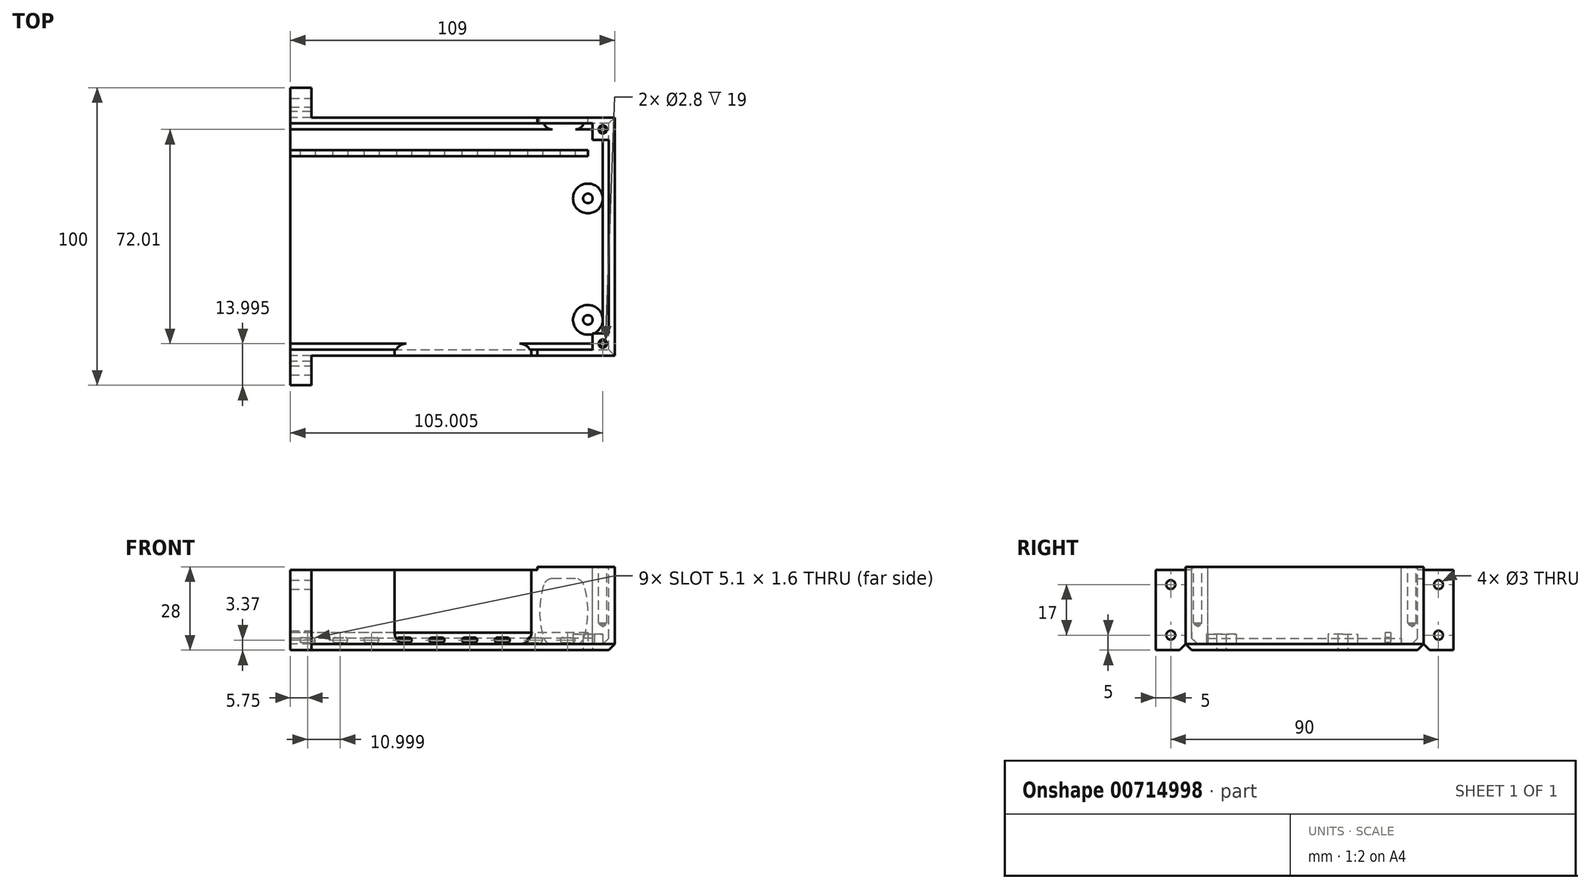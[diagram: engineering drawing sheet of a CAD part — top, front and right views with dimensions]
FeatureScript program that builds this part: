
annotation { "Feature Type Name" : "Feature", "Feature Type Description" : "" }
export const myFeature = defineFeature(function(context is Context, id is Id, definition is map)
    precondition{}
    {
        {
            var Q0;
            Q0=qCreatedBy(makeId("Top.planeOp"),FACE);
            var sketch = newSketch(context, id + "F0", { "sketchPlane" : qUnion([Q0])});
            skLineSegment(sketch, "E0.bottom", {"start": v(54.5, 40) * mm, "end": v(-54.5, 40) * mm});
            skLineSegment(sketch, "E0.top", {"start": v(54.5, -40) * mm, "end": v(-54.5, -40) * mm});
            skLineSegment(sketch, "E0.left", {"start": v(54.5, 40) * mm, "end": v(54.5, -40) * mm});
            skLineSegment(sketch, "E0.right", {"start": v(-54.5, 40) * mm, "end": v(-54.5, -40) * mm});
            skPoint(sketch, "E0.middle", {"position": v(0, 0) * mm});
            skSolve(sketch);
        }
        {
            var Q0;
            Q0=makeQuery(id+"F0.imprint","IMPRINT",FACE,{"disambiguationData":[TD([[makeQuery(id+"F0.imprint","IMPRINT",EDGE,{"derivedFrom":sQuery(id+"F0.wireOp",EDGE,"E0.bottom")}),1.0]])]});
            extrude(context, id + "F1", {"entities" : qUnion([Q0]), "depth" : 27 * mm, "offsetDistance" : 25 * mm});
        }
        {
            var Q0;
            Q0=makeQuery(id+"F1.opExtrude","SWEPT_FACE",FACE,{"disambiguationData":[OSD([sQuery(id+"F0.wireOp",EDGE,"E0.bottom")])]});
            var sketch = newSketch(context, id + "F2", { "sketchPlane" : qUnion([Q0])});
            skLineSegment(sketch, "E1.bottom", {"start": v(-54.5, 27) * mm, "end": v(-47.5, 27) * mm});
            skLineSegment(sketch, "E1.top", {"start": v(-54.5, 0) * mm, "end": v(-47.5, 0) * mm});
            skLineSegment(sketch, "E1.left", {"start": v(-54.5, 27) * mm, "end": v(-54.5, 0) * mm});
            skLineSegment(sketch, "E1.right", {"start": v(-47.5, 27) * mm, "end": v(-47.5, 0) * mm});
            skSolve(sketch);
        }
        {
            var Q0;
            Q0=makeQuery(id+"F2.imprint","IMPRINT",FACE,{"disambiguationData":[TD([[makeQuery(id+"F2.imprint","IMPRINT",EDGE,{"derivedFrom":sQuery(id+"F2.wireOp",EDGE,"E1.bottom")}),-1.0]])]});
            extrude(context, id + "F3", {"entities" : qUnion([Q0]), "operationType" : NewBodyOperationType.ADD, "depth" : 10 * mm, "offsetDistance" : 25 * mm});
        }
        {
            var Q0;
            Q0=makeQuery(id+"F1.opExtrude","SWEPT_FACE",FACE,{"disambiguationData":[OSD([sQuery(id+"F0.wireOp",EDGE,"E0.top")])]});
            var sketch = newSketch(context, id + "F4", { "sketchPlane" : qUnion([Q0])});
            skLineSegment(sketch, "E2.bottom", {"start": v(54.5, 27) * mm, "end": v(47.5, 27) * mm});
            skLineSegment(sketch, "E2.top", {"start": v(54.5, 0) * mm, "end": v(47.5, 0) * mm});
            skLineSegment(sketch, "E2.left", {"start": v(54.5, 27) * mm, "end": v(54.5, 0) * mm});
            skLineSegment(sketch, "E2.right", {"start": v(47.5, 27) * mm, "end": v(47.5, 0) * mm});
            skSolve(sketch);
        }
        {
            var Q0;
            Q0=qSketchRegion(id+"F4",true);
            extrude(context, id + "F5", {"entities" : qUnion([Q0]), "operationType" : NewBodyOperationType.ADD, "depth" : 10 * mm, "offsetDistance" : 25 * mm});
        }
        {
            var Q0;
            Q0=makeQuery(id+"F5.boolean.opBoolean","MERGE",FACE,{"derivedFrom":[makeQuery(id+"F3.boolean.opBoolean","MERGE",FACE,{"derivedFrom":[makeQuery(id+"F1.opExtrude","CAP_FACE",FACE,{"disambiguationData":[OSD([sQuery(id+"F0.wireOp",EDGE,"E0.bottom"),sQuery(id+"F0.wireOp",EDGE,"E0.top"),sQuery(id+"F0.wireOp",EDGE,"E0.left"),sQuery(id+"F0.wireOp",EDGE,"E0.right")])],"isStart":false}),makeQuery(id+"F3.opExtrude","SWEPT_FACE",FACE,{"disambiguationData":[OSD([sQuery(id+"F2.wireOp",EDGE,"E1.bottom")])]})]}),makeQuery(id+"F5.opExtrude","SWEPT_FACE",FACE,{"disambiguationData":[OSD([sQuery(id+"F4.wireOp",EDGE,"E2.bottom")])]})]});
            var sketch = newSketch(context, id + "F6", { "sketchPlane" : qUnion([Q0])});
            skLineSegment(sketch, "E3.0", {"start": v(-52.5, 32.5) * mm, "end": v(-52.5, -32.5) * mm});
            skLineSegment(sketch, "E3.1", {"start": v(52.5, 38) * mm, "end": v(-47, 38) * mm});
            skLineSegment(sketch, "E3.2", {"start": v(-47, -38) * mm, "end": v(54.24, -38) * mm});
            skPoint(sketch, "E4.orphan", {"position": v(49.5, 38) * mm});
            skLineSegment(sketch, "E5.top", {"start": v(-52.5, 32.5) * mm, "end": v(-47, 32.5) * mm});
            skLineSegment(sketch, "E5.right", {"start": v(-47, 38) * mm, "end": v(-47, 32.5) * mm});
            skLineSegment(sketch, "E6.top", {"start": v(-52.5, -32.5) * mm, "end": v(-47, -32.5) * mm});
            skLineSegment(sketch, "E6.right", {"start": v(-47, -38) * mm, "end": v(-47, -32.5) * mm});
            skLineSegment(sketch, "E7", {"start": v(54.24, -38) * mm, "end": v(54.5, -38) * mm});
            skLineSegment(sketch, "E8", {"start": v(52.5, 38) * mm, "end": v(54.5, 38) * mm});
            skSolve(sketch);
        }
        {
            var Q0;
            Q0=makeQuery(id+"F6.imprint","IMPRINT",FACE,{"disambiguationData":[TD([[makeQuery(id+"F6.imprint","IMPRINT",EDGE,{"derivedFrom":sQuery(id+"F6.wireOp",EDGE,"E3.0")}),1.0]])]});
            extrude(context, id + "F7", {"entities" : qUnion([Q0]), "operationType" : NewBodyOperationType.REMOVE, "oppositeDirection" : true, "depth" : 25 * mm, "offsetDistance" : 25 * mm});
        }
        {
            var Q0;
            Q0=makeQuery(id+"F5.boolean.opBoolean","MERGE",FACE,{"derivedFrom":[makeQuery(id+"F3.boolean.opBoolean","MERGE",FACE,{"derivedFrom":[makeQuery(id+"F1.opExtrude","CAP_FACE",FACE,{"disambiguationData":[OSD([sQuery(id+"F0.wireOp",EDGE,"E0.bottom"),sQuery(id+"F0.wireOp",EDGE,"E0.top"),sQuery(id+"F0.wireOp",EDGE,"E0.left"),sQuery(id+"F0.wireOp",EDGE,"E0.right")])],"isStart":true}),makeQuery(id+"F3.opExtrude","SWEPT_FACE",FACE,{"disambiguationData":[OSD([sQuery(id+"F2.wireOp",EDGE,"E1.top")])]})]}),makeQuery(id+"F5.opExtrude","SWEPT_FACE",FACE,{"disambiguationData":[OSD([sQuery(id+"F4.wireOp",EDGE,"E2.top")])]})]});
            var sketch = newSketch(context, id + "F8", { "sketchPlane" : qUnion([Q0])});
            skLineSegment(sketch, "E9.bottom", {"start": v(54.5, 40) * mm, "end": v(-45.5, 40) * mm, "construction": true});
            skLineSegment(sketch, "E9.top", {"start": v(54.5, -40) * mm, "end": v(-45.5, -40) * mm, "construction": true});
            skLineSegment(sketch, "E9.left", {"start": v(54.5, 40) * mm, "end": v(54.5, -40) * mm, "construction": true});
            skLineSegment(sketch, "E9.right", {"start": v(-45.5, 40) * mm, "end": v(-45.5, -40) * mm, "construction": true});
            skLineSegment(sketch, "E10", {"start": v(-45.5, 40) * mm, "end": v(-45.5, 28) * mm, "construction": true});
            skLineSegment(sketch, "E11", {"start": v(-45.5, 40) * mm, "end": v(-45.5, -12.8) * mm, "construction": true});
            skCircle(sketch, "E12", {"center": v(-45.5, 28) * mm, "radius": 1.6 * mm});
            skCircle(sketch, "E13", {"center": v(-45.5, -12.8) * mm, "radius": 1.6 * mm});
            skCircle(sketch, "E14", {"center": v(-45.5, 28) * mm, "radius": 5 * mm});
            skCircle(sketch, "E15", {"center": v(-45.5, -12.8) * mm, "radius": 5 * mm});
            skSolve(sketch);
        }
        {
            var Q0;
            Q0=sQuery(id+"F8.wireOp",VERTEX,"E10.end");
            var Q1;
            Q1=sQuery(id+"F8.wireOp",VERTEX,"E11.end");
            var Q2;
            Q2=makeQuery(id+"F1.opExtrude","SWEPT_BODY",BODY,{"disambiguationData":[OSD([sQuery(id+"F0.wireOp",EDGE,"E0.bottom"),sQuery(id+"F0.wireOp",EDGE,"E0.top"),sQuery(id+"F0.wireOp",EDGE,"E0.left"),sQuery(id+"F0.wireOp",EDGE,"E0.right")])]});
            hole(context, id + "F9", {"style" : HoleStyle.SIMPLE, "endStyle" : HoleEndStyle.THROUGH, "holeDiameter" : 3.2 * mm, "majorDiameter" : 5 * mm, "isTappedThrough" : true, "tappedDepth" : 12 * mm, "tapClearance" : 3, "startFromSketch" : true, "locations" : qUnion([Q0, Q1]), "scope" : qUnion([Q2])});
        }
        {
            var Q0;
            Q0=makeQuery(id+"F7.boolean.opBoolean","COPY",FACE,{"derivedFrom":makeQuery(id+"F7.opExtrude","CAP_FACE",FACE,{"disambiguationData":[OSD([sQuery(id+"F0.wireOp",EDGE,"E0.left"),sQuery(id+"F2.wireOp",EDGE,"E1.bottom"),sQuery(id+"F2.wireOp",EDGE,"E1.left"),sQuery(id+"F4.wireOp",EDGE,"E2.bottom"),sQuery(id+"F4.wireOp",EDGE,"E2.left"),sQuery(id+"F6.wireOp",EDGE,"E3.0"),sQuery(id+"F6.wireOp",EDGE,"E3.1"),sQuery(id+"F6.wireOp",EDGE,"E3.2"),sQuery(id+"F6.wireOp",EDGE,"E5.top"),sQuery(id+"F6.wireOp",EDGE,"E5.right"),sQuery(id+"F6.wireOp",EDGE,"E6.top"),sQuery(id+"F6.wireOp",EDGE,"E6.right"),sQuery(id+"F6.wireOp",EDGE,"E7"),sQuery(id+"F6.wireOp",EDGE,"E8")])],"isStart":false})});
            var sketch = newSketch(context, id + "F10", { "sketchPlane" : qUnion([Q0])});
            skLineSegment(sketch, "E16.bottom", {"start": v(54.5, 38) * mm, "end": v(-47, 38) * mm, "construction": true});
            skLineSegment(sketch, "E16.top", {"start": v(54.5, 29) * mm, "end": v(-47, 29) * mm, "construction": true});
            skLineSegment(sketch, "E16.left", {"start": v(54.5, 38) * mm, "end": v(54.5, 29) * mm, "construction": true});
            skLineSegment(sketch, "E16.right", {"start": v(-47, 38) * mm, "end": v(-47, 29) * mm, "construction": true});
            skLineSegment(sketch, "E17", {"start": v(-52.5, 29) * mm, "end": v(-45.5, 29) * mm, "construction": true});
            skLineSegment(sketch, "E18.bottom", {"start": v(-45.5, 29) * mm, "end": v(54.5, 29) * mm});
            skLineSegment(sketch, "E18.top", {"start": v(-45.5, 27) * mm, "end": v(54.5, 27) * mm});
            skLineSegment(sketch, "E18.left", {"start": v(-45.5, 29) * mm, "end": v(-45.5, 27) * mm});
            skLineSegment(sketch, "E18.right", {"start": v(54.5, 29) * mm, "end": v(54.5, 27) * mm});
            skSolve(sketch);
        }
        {
            var Q0;
            Q0=qSketchRegion(id+"F10",true);
            extrude(context, id + "F11", {"entities" : qUnion([Q0]), "operationType" : NewBodyOperationType.ADD, "depth" : 3.9 * mm, "offsetDistance" : 25 * mm});
        }
        {
            var Q0;
            Q0=makeQuery(id+"F11.opExtrude","SWEPT_FACE",FACE,{"disambiguationData":[OSD([sQuery(id+"F10.wireOp",EDGE,"E18.top")])]});
            var sketch = newSketch(context, id + "F12", { "sketchPlane" : qUnion([Q0])});
            skLineSegment(sketch, "E19.bottom", {"start": v(54.5, 5.9) * mm, "end": v(-45.5, 5.9) * mm, "construction": true});
            skLineSegment(sketch, "E19.top", {"start": v(54.5, 3.37) * mm, "end": v(-45.5, 3.37) * mm, "construction": true});
            skLineSegment(sketch, "E19.left", {"start": v(54.5, 5.9) * mm, "end": v(54.5, 3.37) * mm, "construction": true});
            skLineSegment(sketch, "E19.right", {"start": v(-45.5, 5.9) * mm, "end": v(-45.5, 3.37) * mm, "construction": true});
            skLineSegment(sketch, "E20", {"start": v(54.5, 3.37) * mm, "end": v(48.75, 3.37) * mm, "construction": true});
            skLineSegment(sketch, "E21.bottom", {"start": v(50.5, 4.17) * mm, "end": v(47, 4.17) * mm});
            skLineSegment(sketch, "E21.top", {"start": v(50.5, 2.57) * mm, "end": v(47, 2.57) * mm});
            skPoint(sketch, "E21.middle", {"position": v(48.75, 3.37) * mm});
            skArc(sketch, "E22", {"start": v(47, 4.17) * mm, "mid": v(46.2, 3.37) * mm, "end": v(47, 2.57) * mm});
            skArc(sketch, "E23", {"start": v(50.5, 2.57) * mm, "mid": v(51.3, 3.37) * mm, "end": v(50.5, 4.17) * mm});
            skLineSegment(sketch, "E24", {"start": v(48.75, 3.37) * mm, "end": v(37.75, 3.37) * mm, "construction": true});
            skLineSegment(sketch, "E25.bottom", {"start": v(39.5, 4.17) * mm, "end": v(36, 4.17) * mm});
            skLineSegment(sketch, "E25.top", {"start": v(39.5, 2.57) * mm, "end": v(36, 2.57) * mm});
            skPoint(sketch, "E25.middle", {"position": v(37.75, 3.37) * mm});
            skArc(sketch, "E26", {"start": v(36, 4.17) * mm, "mid": v(35.2, 3.37) * mm, "end": v(36, 2.57) * mm});
            skArc(sketch, "E27", {"start": v(39.5, 2.57) * mm, "mid": v(40.3, 3.37) * mm, "end": v(39.5, 4.17) * mm});
            skLineSegment(sketch, "E28", {"start": v(37.75, 3.37) * mm, "end": v(26.75, 3.37) * mm, "construction": true});
            skLineSegment(sketch, "E29", {"start": v(26.75, 3.37) * mm, "end": v(15.75, 3.37) * mm, "construction": true});
            skLineSegment(sketch, "E30", {"start": v(15.75, 3.37) * mm, "end": v(4.75, 3.37) * mm, "construction": true});
            skLineSegment(sketch, "E31", {"start": v(4.75, 3.37) * mm, "end": v(-6.25, 3.37) * mm, "construction": true});
            skLineSegment(sketch, "E32", {"start": v(-6.25, 3.37) * mm, "end": v(-17.25, 3.37) * mm, "construction": true});
            skLineSegment(sketch, "E33", {"start": v(-17.25, 3.37) * mm, "end": v(-28.25, 3.37) * mm, "construction": true});
            skLineSegment(sketch, "E34", {"start": v(-28.25, 3.37) * mm, "end": v(-39.25, 3.37) * mm, "construction": true});
            skLineSegment(sketch, "E35.bottom", {"start": v(29.03, 4.17) * mm, "end": v(25.53, 4.17) * mm});
            skLineSegment(sketch, "E35.top", {"start": v(29.03, 2.57) * mm, "end": v(25.53, 2.57) * mm});
            skPoint(sketch, "E35.middle", {"position": v(27.28, 3.37) * mm});
            skArc(sketch, "E36", {"start": v(25.53, 4.17) * mm, "mid": v(24.73, 3.37) * mm, "end": v(25.53, 2.57) * mm});
            skArc(sketch, "E37", {"start": v(29.03, 2.57) * mm, "mid": v(29.83, 3.37) * mm, "end": v(29.03, 4.17) * mm});
            skLineSegment(sketch, "E38.bottom", {"start": v(18.03, 4.17) * mm, "end": v(14.53, 4.17) * mm});
            skLineSegment(sketch, "E38.top", {"start": v(18.03, 2.57) * mm, "end": v(14.53, 2.57) * mm});
            skPoint(sketch, "E38.middle", {"position": v(16.28, 3.37) * mm});
            skArc(sketch, "E39", {"start": v(14.53, 4.17) * mm, "mid": v(13.73, 3.37) * mm, "end": v(14.53, 2.57) * mm});
            skArc(sketch, "E40", {"start": v(18.03, 2.57) * mm, "mid": v(18.83, 3.37) * mm, "end": v(18.03, 4.17) * mm});
            skLineSegment(sketch, "E41.bottom", {"start": v(7.03, 4.17) * mm, "end": v(3.53, 4.17) * mm});
            skLineSegment(sketch, "E41.top", {"start": v(7.03, 2.57) * mm, "end": v(3.53, 2.57) * mm});
            skPoint(sketch, "E41.middle", {"position": v(5.28, 3.37) * mm});
            skArc(sketch, "E42", {"start": v(3.53, 4.17) * mm, "mid": v(2.73, 3.37) * mm, "end": v(3.53, 2.57) * mm});
            skArc(sketch, "E43", {"start": v(7.03, 2.57) * mm, "mid": v(7.83, 3.37) * mm, "end": v(7.03, 4.17) * mm});
            skLineSegment(sketch, "E44.bottom", {"start": v(-3.97, 4.17) * mm, "end": v(-7.47, 4.17) * mm});
            skLineSegment(sketch, "E44.top", {"start": v(-3.97, 2.57) * mm, "end": v(-7.47, 2.57) * mm});
            skPoint(sketch, "E44.middle", {"position": v(-5.72, 3.37) * mm});
            skArc(sketch, "E45", {"start": v(-7.47, 4.17) * mm, "mid": v(-8.27, 3.37) * mm, "end": v(-7.47, 2.57) * mm});
            skArc(sketch, "E46", {"start": v(-3.97, 2.57) * mm, "mid": v(-3.17, 3.37) * mm, "end": v(-3.97, 4.17) * mm});
            skLineSegment(sketch, "E47.bottom", {"start": v(-14.97, 4.17) * mm, "end": v(-18.47, 4.17) * mm});
            skLineSegment(sketch, "E47.top", {"start": v(-14.97, 2.57) * mm, "end": v(-18.47, 2.57) * mm});
            skPoint(sketch, "E47.middle", {"position": v(-16.72, 3.37) * mm});
            skArc(sketch, "E48", {"start": v(-18.47, 4.17) * mm, "mid": v(-19.27, 3.37) * mm, "end": v(-18.47, 2.57) * mm});
            skArc(sketch, "E49", {"start": v(-14.97, 2.57) * mm, "mid": v(-14.17, 3.37) * mm, "end": v(-14.97, 4.17) * mm});
            skLineSegment(sketch, "E50.bottom", {"start": v(-25.97, 4.17) * mm, "end": v(-29.47, 4.17) * mm});
            skLineSegment(sketch, "E50.top", {"start": v(-25.97, 2.57) * mm, "end": v(-29.47, 2.57) * mm});
            skPoint(sketch, "E50.middle", {"position": v(-27.72, 3.37) * mm});
            skArc(sketch, "E51", {"start": v(-29.47, 4.17) * mm, "mid": v(-30.27, 3.37) * mm, "end": v(-29.47, 2.57) * mm});
            skArc(sketch, "E52", {"start": v(-25.97, 2.57) * mm, "mid": v(-25.17, 3.37) * mm, "end": v(-25.97, 4.17) * mm});
            skLineSegment(sketch, "E53.bottom", {"start": v(-36.97, 4.17) * mm, "end": v(-40.47, 4.17) * mm});
            skLineSegment(sketch, "E53.top", {"start": v(-36.97, 2.57) * mm, "end": v(-40.47, 2.57) * mm});
            skPoint(sketch, "E53.middle", {"position": v(-38.72, 3.37) * mm});
            skArc(sketch, "E54", {"start": v(-40.47, 4.17) * mm, "mid": v(-41.27, 3.37) * mm, "end": v(-40.47, 2.57) * mm});
            skArc(sketch, "E55", {"start": v(-36.97, 2.57) * mm, "mid": v(-36.17, 3.37) * mm, "end": v(-36.97, 4.17) * mm});
            skSolve(sketch);
        }
        {
            var Q0;
            Q0=makeQuery(id+"F12.imprint","IMPRINT",FACE,{"disambiguationData":[TD([[makeQuery(id+"F12.imprint","IMPRINT",EDGE,{"derivedFrom":sQuery(id+"F12.wireOp",EDGE,"E53.bottom")}),1.0]])]});
            var Q1;
            Q1=makeQuery(id+"F12.imprint","IMPRINT",FACE,{"disambiguationData":[TD([[makeQuery(id+"F12.imprint","IMPRINT",EDGE,{"derivedFrom":sQuery(id+"F12.wireOp",EDGE,"E50.bottom")}),1.0]])]});
            var Q2;
            Q2=makeQuery(id+"F12.imprint","IMPRINT",FACE,{"disambiguationData":[TD([[makeQuery(id+"F12.imprint","IMPRINT",EDGE,{"derivedFrom":sQuery(id+"F12.wireOp",EDGE,"E47.bottom")}),1.0]])]});
            var Q3;
            Q3=makeQuery(id+"F12.imprint","IMPRINT",FACE,{"disambiguationData":[TD([[makeQuery(id+"F12.imprint","IMPRINT",EDGE,{"derivedFrom":sQuery(id+"F12.wireOp",EDGE,"E44.bottom")}),1.0]])]});
            var Q4;
            Q4=makeQuery(id+"F12.imprint","IMPRINT",FACE,{"disambiguationData":[TD([[makeQuery(id+"F12.imprint","IMPRINT",EDGE,{"derivedFrom":sQuery(id+"F12.wireOp",EDGE,"E41.bottom")}),1.0]])]});
            var Q5;
            Q5=makeQuery(id+"F12.imprint","IMPRINT",FACE,{"disambiguationData":[TD([[makeQuery(id+"F12.imprint","IMPRINT",EDGE,{"derivedFrom":sQuery(id+"F12.wireOp",EDGE,"E38.bottom")}),1.0]])]});
            var Q6;
            Q6=makeQuery(id+"F12.imprint","IMPRINT",FACE,{"disambiguationData":[TD([[makeQuery(id+"F12.imprint","IMPRINT",EDGE,{"derivedFrom":sQuery(id+"F12.wireOp",EDGE,"E35.bottom")}),1.0]])]});
            var Q7;
            Q7=makeQuery(id+"F12.imprint","IMPRINT",FACE,{"disambiguationData":[TD([[makeQuery(id+"F12.imprint","IMPRINT",EDGE,{"derivedFrom":sQuery(id+"F12.wireOp",EDGE,"E25.bottom")}),1.0]])]});
            var Q8;
            Q8=makeQuery(id+"F12.imprint","IMPRINT",FACE,{"disambiguationData":[TD([[makeQuery(id+"F12.imprint","IMPRINT",EDGE,{"derivedFrom":sQuery(id+"F12.wireOp",EDGE,"E21.bottom")}),1.0]])]});
            extrude(context, id + "F13", {"entities" : qUnion([Q0, Q1, Q2, Q3, Q4, Q5, Q6, Q7, Q8]), "operationType" : NewBodyOperationType.REMOVE, "endBound" : BoundingType.UP_TO_NEXT, "oppositeDirection" : true, "depth" : 25 * mm, "offsetDistance" : 25 * mm});
        }
        {
            var Q0;
            Q0=makeQuery(id+"F7.boolean.opBoolean","COPY",FACE,{"derivedFrom":makeQuery(id+"F7.opExtrude","CAP_FACE",FACE,{"disambiguationData":[OSD([sQuery(id+"F0.wireOp",EDGE,"E0.left"),sQuery(id+"F2.wireOp",EDGE,"E1.bottom"),sQuery(id+"F2.wireOp",EDGE,"E1.left"),sQuery(id+"F4.wireOp",EDGE,"E2.bottom"),sQuery(id+"F4.wireOp",EDGE,"E2.left"),sQuery(id+"F6.wireOp",EDGE,"E3.0"),sQuery(id+"F6.wireOp",EDGE,"E3.1"),sQuery(id+"F6.wireOp",EDGE,"E3.2"),sQuery(id+"F6.wireOp",EDGE,"E5.top"),sQuery(id+"F6.wireOp",EDGE,"E5.right"),sQuery(id+"F6.wireOp",EDGE,"E6.top"),sQuery(id+"F6.wireOp",EDGE,"E6.right"),sQuery(id+"F6.wireOp",EDGE,"E7"),sQuery(id+"F6.wireOp",EDGE,"E8")])],"isStart":false})});
            var sketch = newSketch(context, id + "F14", { "sketchPlane" : qUnion([Q0])});
            skCircle(sketch, "E56", {"center": v(-45.5, 12.8) * mm, "radius": 5 * mm});
            skCircle(sketch, "E57", {"center": v(-45.5, -28) * mm, "radius": 5 * mm});
            skCircle(sketch, "E58", {"center": v(-45.5, -28) * mm, "radius": 1.6 * mm});
            skCircle(sketch, "E59", {"center": v(-45.5, 12.8) * mm, "radius": 1.6 * mm});
            skSolve(sketch);
        }
        {
            var Q0;
            Q0=qSketchRegion(id+"F14",true);
            extrude(context, id + "F15", {"entities" : qUnion([Q0]), "operationType" : NewBodyOperationType.ADD, "depth" : 3.4 * mm, "offsetDistance" : 25 * mm});
        }
        {
            var Q0;
            Q0=makeQuery(id+"F7.boolean.opBoolean","COPY",EDGE,{"derivedFrom":makeQuery(id+"F7.opExtrude","CAP_EDGE",EDGE,{"disambiguationData":[OSD([sQuery(id+"F6.wireOp",EDGE,"E3.0")])],"isStart":false})});
            var Q1;
            Q1=makeQuery(id+"F1.opExtrude","CAP_EDGE",EDGE,{"disambiguationData":[OSD([sQuery(id+"F0.wireOp",EDGE,"E0.right")])],"isStart":true});
            var Q2;
            Q2=makeQuery(id+"F1.opExtrude","CAP_EDGE",EDGE,{"disambiguationData":[OSD([sQuery(id+"F0.wireOp",EDGE,"E0.top")])],"isStart":true});
            var Q3;
            Q3=makeQuery(id+"F1.opExtrude","CAP_EDGE",EDGE,{"disambiguationData":[OSD([sQuery(id+"F0.wireOp",EDGE,"E0.bottom")])],"isStart":true});
            var Q4;
            Q4=makeQuery(id+"F7.boolean.opBoolean","COPY",EDGE,{"derivedFrom":makeQuery(id+"F7.opExtrude","CAP_EDGE",EDGE,{"disambiguationData":[OSD([sQuery(id+"F6.wireOp",EDGE,"E3.1"),sQuery(id+"F6.wireOp",EDGE,"E8")])],"isStart":false})});
            chamfer(context, id + "F16", {"entities" : qUnion([Q0, Q1, Q2, Q3, Q4]), "width" : 2 * mm, "tangentPropagation" : true});
        }
        {
            var Q0;
            Q0=makeQuery(id+"F11.boolean.opBoolean","MERGE",FACE,{"derivedFrom":[makeQuery(id+"F5.boolean.opBoolean","MERGE",FACE,{"derivedFrom":[makeQuery(id+"F3.boolean.opBoolean","MERGE",FACE,{"derivedFrom":[makeQuery(id+"F1.opExtrude","SWEPT_FACE",FACE,{"disambiguationData":[OSD([sQuery(id+"F0.wireOp",EDGE,"E0.left")])]}),makeQuery(id+"F3.opExtrude","SWEPT_FACE",FACE,{"disambiguationData":[OSD([sQuery(id+"F2.wireOp",EDGE,"E1.left")])]})]}),makeQuery(id+"F5.opExtrude","SWEPT_FACE",FACE,{"disambiguationData":[OSD([sQuery(id+"F4.wireOp",EDGE,"E2.left")])]})]}),makeQuery(id+"F11.opExtrude","SWEPT_FACE",FACE,{"disambiguationData":[OSD([sQuery(id+"F10.wireOp",EDGE,"E18.right")])]})]});
            var sketch = newSketch(context, id + "F17", { "sketchPlane" : qUnion([Q0])});
            skLineSegment(sketch, "E60.bottom", {"start": v(38, 0) * mm, "end": v(42, 0) * mm});
            skLineSegment(sketch, "E60.top", {"start": v(38, 2) * mm, "end": v(42, 2) * mm, "construction": true});
            skLineSegment(sketch, "E60.left", {"start": v(38, 0) * mm, "end": v(38, 2) * mm, "construction": true});
            skLineSegment(sketch, "E60.right", {"start": v(42, 0) * mm, "end": v(42, 2) * mm, "construction": true});
            skLineSegment(sketch, "E61", {"start": v(42, 0) * mm, "end": v(40, 2) * mm});
            skLineSegment(sketch, "E62", {"start": v(40, 2) * mm, "end": v(38, 0) * mm});
            skLineSegment(sketch, "E63.bottom", {"start": v(-38, 0) * mm, "end": v(-42.01, 0) * mm});
            skLineSegment(sketch, "E63.top", {"start": v(-38, 2) * mm, "end": v(-42.01, 2) * mm, "construction": true});
            skLineSegment(sketch, "E63.left", {"start": v(-38, 0) * mm, "end": v(-38, 2) * mm, "construction": true});
            skLineSegment(sketch, "E63.right", {"start": v(-42.01, 0) * mm, "end": v(-42.01, 2) * mm, "construction": true});
            skLineSegment(sketch, "E64", {"start": v(-38, 0) * mm, "end": v(-40, 2) * mm});
            skLineSegment(sketch, "E65", {"start": v(-40, 2) * mm, "end": v(-42.01, 0) * mm});
            skSolve(sketch);
        }
        {
            var Q0;
            Q0=qSketchRegion(id+"F17",true);
            extrude(context, id + "F18", {"entities" : qUnion([Q0]), "operationType" : NewBodyOperationType.REMOVE, "oppositeDirection" : true, "depth" : 7 * mm, "offsetDistance" : 25 * mm});
        }
        {
            var Q0;
            Q0=makeQuery(id+"F3.opExtrude","SWEPT_FACE",FACE,{"disambiguationData":[OSD([sQuery(id+"F2.wireOp",EDGE,"E1.right")])]});
            var sketch = newSketch(context, id + "F19", { "sketchPlane" : qUnion([Q0])});
            skLineSegment(sketch, "E66.bottom", {"start": v(-50, 27) * mm, "end": v(-45, 27) * mm, "construction": true});
            skLineSegment(sketch, "E66.top", {"start": v(-50, 22) * mm, "end": v(-45, 22) * mm, "construction": true});
            skLineSegment(sketch, "E66.left", {"start": v(-50, 27) * mm, "end": v(-50, 22) * mm, "construction": true});
            skLineSegment(sketch, "E66.right", {"start": v(-45, 27) * mm, "end": v(-45, 22) * mm, "construction": true});
            skLineSegment(sketch, "E67.left", {"start": v(-50, 27) * mm, "end": v(-50, 8.94) * mm, "construction": true});
            skLineSegment(sketch, "E68.bottom", {"start": v(-50, 22) * mm, "end": v(-45, 22) * mm});
            skLineSegment(sketch, "E68.top", {"start": v(-50, 5) * mm, "end": v(-45, 5) * mm, "construction": true});
            skLineSegment(sketch, "E68.left", {"start": v(-50, 22) * mm, "end": v(-50, 5) * mm, "construction": true});
            skLineSegment(sketch, "E68.right", {"start": v(-45, 22) * mm, "end": v(-45, 5) * mm, "construction": true});
            skSolve(sketch);
        }
        {
            var Q0;
            Q0=sQuery(id+"F19.wireOp",VERTEX,"E66.right.end");
            var Q1;
            Q1=sQuery(id+"F19.wireOp",VERTEX,"E68.right.end");
            var Q2;
            Q2=makeQuery(id+"F1.opExtrude","SWEPT_BODY",BODY,{"disambiguationData":[OSD([sQuery(id+"F0.wireOp",EDGE,"E0.bottom"),sQuery(id+"F0.wireOp",EDGE,"E0.top"),sQuery(id+"F0.wireOp",EDGE,"E0.left"),sQuery(id+"F0.wireOp",EDGE,"E0.right")])]});
            hole(context, id + "F20", {"style" : HoleStyle.SIMPLE, "endStyle" : HoleEndStyle.THROUGH, "holeDiameter" : 3 * mm, "majorDiameter" : 5 * mm, "isTappedThrough" : true, "tappedDepth" : 12 * mm, "tapClearance" : 3, "startFromSketch" : true, "locations" : qUnion([Q0, Q1]), "scope" : qUnion([Q2])});
        }
        {
            var Q0;
            Q0=makeQuery(id+"F5.opExtrude","SWEPT_FACE",FACE,{"disambiguationData":[OSD([sQuery(id+"F4.wireOp",EDGE,"E2.right")])]});
            var sketch = newSketch(context, id + "F21", { "sketchPlane" : qUnion([Q0])});
            skLineSegment(sketch, "E69.bottom", {"start": v(50, 27) * mm, "end": v(45, 27) * mm, "construction": true});
            skLineSegment(sketch, "E69.top", {"start": v(50, 22) * mm, "end": v(45, 22) * mm, "construction": true});
            skLineSegment(sketch, "E69.left", {"start": v(50, 27) * mm, "end": v(50, 22) * mm, "construction": true});
            skLineSegment(sketch, "E69.right", {"start": v(45, 27) * mm, "end": v(45, 22) * mm, "construction": true});
            skLineSegment(sketch, "E70.top", {"start": v(50, 5) * mm, "end": v(45, 5) * mm, "construction": true});
            skLineSegment(sketch, "E70.left", {"start": v(50, 22) * mm, "end": v(50, 5) * mm, "construction": true});
            skLineSegment(sketch, "E70.right", {"start": v(45, 22) * mm, "end": v(45, 5) * mm, "construction": true});
            skSolve(sketch);
        }
        {
            var Q0;
            Q0=sQuery(id+"F21.wireOp",VERTEX,"E69.top.end");
            var Q1;
            Q1=sQuery(id+"F21.wireOp",VERTEX,"E70.top.end");
            var Q2;
            Q2=makeQuery(id+"F1.opExtrude","SWEPT_BODY",BODY,{"disambiguationData":[OSD([sQuery(id+"F0.wireOp",EDGE,"E0.bottom"),sQuery(id+"F0.wireOp",EDGE,"E0.top"),sQuery(id+"F0.wireOp",EDGE,"E0.left"),sQuery(id+"F0.wireOp",EDGE,"E0.right")])]});
            hole(context, id + "F22", {"style" : HoleStyle.SIMPLE, "endStyle" : HoleEndStyle.THROUGH, "holeDiameter" : 3 * mm, "majorDiameter" : 5 * mm, "isTappedThrough" : true, "tappedDepth" : 12 * mm, "tapClearance" : 3, "startFromSketch" : true, "locations" : qUnion([Q0, Q1]), "scope" : qUnion([Q2])});
        }
        {
            var Q0;
            Q0=makeQuery(id+"F1.opExtrude","SWEPT_BODY",BODY,{"disambiguationData":[OSD([sQuery(id+"F0.wireOp",EDGE,"E0.bottom"),sQuery(id+"F0.wireOp",EDGE,"E0.top"),sQuery(id+"F0.wireOp",EDGE,"E0.left"),sQuery(id+"F0.wireOp",EDGE,"E0.right")])]});
            var Q1;
            Q1=makeQuery(id+"F11.boolean.opBoolean","MERGE",FACE,{"derivedFrom":[makeQuery(id+"F5.boolean.opBoolean","MERGE",FACE,{"derivedFrom":[makeQuery(id+"F3.boolean.opBoolean","MERGE",FACE,{"derivedFrom":[makeQuery(id+"F1.opExtrude","SWEPT_FACE",FACE,{"disambiguationData":[OSD([sQuery(id+"F0.wireOp",EDGE,"E0.left")])]}),makeQuery(id+"F3.opExtrude","SWEPT_FACE",FACE,{"disambiguationData":[OSD([sQuery(id+"F2.wireOp",EDGE,"E1.left")])]})]}),makeQuery(id+"F5.opExtrude","SWEPT_FACE",FACE,{"disambiguationData":[OSD([sQuery(id+"F4.wireOp",EDGE,"E2.left")])]})]}),makeQuery(id+"F11.opExtrude","SWEPT_FACE",FACE,{"disambiguationData":[OSD([sQuery(id+"F10.wireOp",EDGE,"E18.right")])]})]});
            mirror(context, id + "F23", {"entities" : qUnion([Q0]), "mirrorPlane" : qUnion([Q1])});
        }
        {
            var Q0;
            Q0=makeQuery(id+"F1.opExtrude","SWEPT_BODY",BODY,{"disambiguationData":[OSD([sQuery(id+"F0.wireOp",EDGE,"E0.bottom"),sQuery(id+"F0.wireOp",EDGE,"E0.top"),sQuery(id+"F0.wireOp",EDGE,"E0.left"),sQuery(id+"F0.wireOp",EDGE,"E0.right")])]});
            deleteBodies(context, id + "F24", {"entities" : qUnion([Q0])});
        }
        {
            var Q0;
            Q0=makeQuery(id+"F23.opPattern","COPY",FACE,{"derivedFrom":makeQuery(id+"F5.boolean.opBoolean","MERGE",FACE,{"derivedFrom":[makeQuery(id+"F3.boolean.opBoolean","MERGE",FACE,{"derivedFrom":[makeQuery(id+"F1.opExtrude","CAP_FACE",FACE,{"disambiguationData":[OSD([sQuery(id+"F0.wireOp",EDGE,"E0.bottom"),sQuery(id+"F0.wireOp",EDGE,"E0.top"),sQuery(id+"F0.wireOp",EDGE,"E0.left"),sQuery(id+"F0.wireOp",EDGE,"E0.right")])],"isStart":false}),makeQuery(id+"F3.opExtrude","SWEPT_FACE",FACE,{"disambiguationData":[OSD([sQuery(id+"F2.wireOp",EDGE,"E1.bottom")])]})]}),makeQuery(id+"F5.opExtrude","SWEPT_FACE",FACE,{"disambiguationData":[OSD([sQuery(id+"F4.wireOp",EDGE,"E2.bottom")])]})]}),"instanceName":"1"});
            var sketch = newSketch(context, id + "F25", { "sketchPlane" : qUnion([Q0])});
            skLineSegment(sketch, "E71.bottom", {"start": v(163.5, -40) * mm, "end": v(137.5, -40) * mm, "construction": true});
            skLineSegment(sketch, "E71.top", {"start": v(163.5, -40) * mm, "end": v(137.5, -40) * mm, "construction": true});
            skLineSegment(sketch, "E71.left", {"start": v(163.5, -40) * mm, "end": v(163.5, -40) * mm});
            skLineSegment(sketch, "E71.right", {"start": v(137.5, -40) * mm, "end": v(137.5, -40) * mm});
            skLineSegment(sketch, "E72.bottom", {"start": v(163.5, 40) * mm, "end": v(137.5, 40) * mm, "construction": true});
            skLineSegment(sketch, "E72.top", {"start": v(163.5, 40) * mm, "end": v(137.5, 40) * mm, "construction": true});
            skLineSegment(sketch, "E72.left", {"start": v(163.5, 40) * mm, "end": v(163.5, 40) * mm});
            skLineSegment(sketch, "E72.right", {"start": v(137.5, 40) * mm, "end": v(137.5, 40) * mm});
            skLineSegment(sketch, "E73", {"start": v(137.5, 40) * mm, "end": v(137.5, 38) * mm});
            skPoint(sketch, "E73.endSnap0", {"position": v(105.25, 38) * mm});
            skLineSegment(sketch, "E74", {"start": v(137.5, -40) * mm, "end": v(137.5, -38) * mm});
            skSolve(sketch);
        }
        {
            var Q0;
            Q0 = qSketchRegion(id + "F25", true);
            var Q1;
            {var subQ4=sQuery(id+"F25.wireOp",EDGE,"E73");Q1=makeQuery(id+"F25.imprint","IMPRINT",FACE,{"disambiguationData":[TD([[makeQuery(id+"F25.imprint","IMPRINT",EDGE,{"derivedFrom":subQ4}),1.0]])]});}
            extrude(context, id + "F26", {"entities" : qUnion([Q0, Q1]), "operationType" : NewBodyOperationType.ADD, "depth" : 1 * mm, "offsetDistance" : 25 * mm});
        }
        {
            var Q0;
            {var subQ0=sQuery(id+"F0.wireOp",EDGE,"E0.bottom");Q0=makeQuery(id+"F26.boolean.opBoolean","MERGE",FACE,{"derivedFrom":[makeQuery(id+"F23.opPattern","COPY",FACE,{"derivedFrom":makeQuery(id+"F1.opExtrude","SWEPT_FACE",FACE,{"disambiguationData":[OSD([subQ0])]}),"instanceName":"1"}),makeQuery(id+"F26.opExtrude","SWEPT_FACE",FACE,{"disambiguationData":[OSD([subQ0])]})]});}
            var sketch = newSketch(context, id + "F27", { "sketchPlane" : qUnion([Q0])});
            skLineSegment(sketch, "E75.bottom", {"start": v(-163.5, 28) * mm, "end": v(-152.4, 28) * mm, "construction": true});
            skLineSegment(sketch, "E75.top", {"start": v(-163.5, 2) * mm, "end": v(-152.4, 2) * mm, "construction": true});
            skLineSegment(sketch, "E75.left", {"start": v(-163.5, 28) * mm, "end": v(-163.5, 2) * mm, "construction": true});
            skLineSegment(sketch, "E75.right", {"start": v(-152.4, 28) * mm, "end": v(-152.4, 24) * mm, "construction": true});
            skLineSegment(sketch, "E76.bottom", {"start": v(-152.4, 2) * mm, "end": v(-140.4, 2) * mm});
            skLineSegment(sketch, "E76.top", {"start": v(-152.4, 24) * mm, "end": v(-140.4, 24) * mm});
            skArc(sketch, "E77", {"start": v(-152.4, 24) * mm, "mid": v(-154.49, 13) * mm, "end": v(-152.4, 2) * mm});
            skArc(sketch, "E78", {"start": v(-140.4, 2) * mm, "mid": v(-138.31, 13) * mm, "end": v(-140.4, 24) * mm});
            skSolve(sketch);
        }
        {
            var Q0;
            Q0 = qSketchRegion(id + "F27", true);
            extrude(context, id + "F28", {"entities" : qUnion([Q0]), "operationType" : NewBodyOperationType.REMOVE, "endBound" : BoundingType.UP_TO_NEXT, "oppositeDirection" : true, "depth" : 25 * mm, "offsetDistance" : 25 * mm});
        }
        {
            var Q0;
            Q0=makeQuery(id+"F28.boolean.opBoolean","COPY",EDGE,{"derivedFrom":makeQuery(id+"F28.opExtrude","SWEPT_EDGE",EDGE,{"disambiguationData":[OSD([sQuery(id+"F27.wireOp",EDGE,"E76.top"),sQuery(id+"F27.wireOp",EDGE,"E77")])]})});
            var Q1;
            Q1=makeQuery(id+"F28.boolean.opBoolean","COPY",EDGE,{"derivedFrom":makeQuery(id+"F28.opExtrude","SWEPT_EDGE",EDGE,{"disambiguationData":[OSD([sQuery(id+"F27.wireOp",EDGE,"E76.top"),sQuery(id+"F27.wireOp",EDGE,"E78")])]})});
            var Q2;
            Q2=makeQuery(id+"F28.boolean.opBoolean","COPY",EDGE,{"derivedFrom":makeQuery(id+"F28.opExtrude","SWEPT_EDGE",EDGE,{"disambiguationData":[OSD([sQuery(id+"F0.wireOp",EDGE,"E0.bottom"),sQuery(id+"F27.wireOp",EDGE,"E76.bottom"),sQuery(id+"F27.wireOp",EDGE,"E78")])]})});
            var Q3;
            Q3=makeQuery(id+"F28.boolean.opBoolean","COPY",EDGE,{"derivedFrom":makeQuery(id+"F28.opExtrude","SWEPT_EDGE",EDGE,{"disambiguationData":[OSD([sQuery(id+"F0.wireOp",EDGE,"E0.bottom"),sQuery(id+"F27.wireOp",EDGE,"E76.bottom"),sQuery(id+"F27.wireOp",EDGE,"E77")])]})});
            fillet(context, id + "F29", {"entities" : qUnion([Q0, Q1, Q2, Q3]), "radius" : 3 * mm, "tangentPropagation" : true, "allowEdgeOverflow" : false});
        }
        {
            var Q0;
            {var subQ1=sQuery(id+"F0.wireOp",EDGE,"E0.top");var subQ5=sQuery(id+"F4.wireOp",EDGE,"E2.bottom");var subQ6=sQuery(id+"F0.wireOp",EDGE,"E0.left");Q0=makeQuery(id+"F26.boolean.opBoolean","SPLIT",FACE,{"disambiguationData":[TD([makeQuery(id+"F23.opPattern","COPY",FACE,{"derivedFrom":makeQuery(id+"F1.opExtrude","SWEPT_FACE",FACE,{"disambiguationData":[OSD([subQ1])]}),"instanceName":"1"})])],"derivedFrom":makeQuery(id+"F23.opPattern","COPY",FACE,{"derivedFrom":makeQuery(id+"F5.boolean.opBoolean","MERGE",FACE,{"derivedFrom":[makeQuery(id+"F3.boolean.opBoolean","MERGE",FACE,{"derivedFrom":[makeQuery(id+"F1.opExtrude","CAP_FACE",FACE,{"disambiguationData":[OSD([sQuery(id+"F0.wireOp",EDGE,"E0.bottom"),subQ1,subQ6,sQuery(id+"F0.wireOp",EDGE,"E0.right")])],"isStart":false}),makeQuery(id+"F3.opExtrude","SWEPT_FACE",FACE,{"disambiguationData":[OSD([sQuery(id+"F2.wireOp",EDGE,"E1.bottom")])]})]}),makeQuery(id+"F5.opExtrude","SWEPT_FACE",FACE,{"disambiguationData":[OSD([subQ5])]})]}),"instanceName":"1"})});}
            var sketch = newSketch(context, id + "F30", { "sketchPlane" : qUnion([Q0])});
            skLineSegment(sketch, "E79.bottom", {"start": v(137.5, -40) * mm, "end": v(135.5, -40) * mm, "construction": true});
            skLineSegment(sketch, "E79.top", {"start": v(137.5, -38) * mm, "end": v(135.5, -38) * mm, "construction": true});
            skLineSegment(sketch, "E79.left", {"start": v(137.5, -40) * mm, "end": v(137.5, -38) * mm, "construction": true});
            skLineSegment(sketch, "E79.right", {"start": v(135.5, -40) * mm, "end": v(135.5, -38) * mm, "construction": true});
            skLineSegment(sketch, "E80.bottom", {"start": v(135.5, -38) * mm, "end": v(89.5, -38) * mm});
            skLineSegment(sketch, "E80.top", {"start": v(135.5, -40) * mm, "end": v(89.5, -40) * mm});
            skLineSegment(sketch, "E80.left", {"start": v(135.5, -38) * mm, "end": v(135.5, -40) * mm});
            skLineSegment(sketch, "E80.right", {"start": v(89.5, -38) * mm, "end": v(89.5, -40) * mm});
            skSolve(sketch);
        }
        {
            var Q0;
            Q0 = qSketchRegion(id + "F30", true);
            extrude(context, id + "F31", {"entities" : qUnion([Q0]), "operationType" : NewBodyOperationType.REMOVE, "oppositeDirection" : true, "depth" : 25 * mm, "offsetDistance" : 25 * mm});
        }
        {
            var Q0;
            {var subQ3=sQuery(id+"F6.wireOp",EDGE,"E7");var subQ4=sQuery(id+"F6.wireOp",EDGE,"E3.2");var subQ5=sQuery(id+"F30.wireOp",EDGE,"E80.right");Q0=makeQuery(id+"F31.boolean.opBoolean","SPLIT",EDGE,{"disambiguationData":[TD([makeQuery(id+"F31.opExtrude","SWEPT_FACE",FACE,{"disambiguationData":[OSD([subQ5])]})])],"derivedFrom":makeQuery(id+"F23.opPattern","COPY",EDGE,{"derivedFrom":makeQuery(id+"F7.boolean.opBoolean","COPY",EDGE,{"derivedFrom":makeQuery(id+"F7.opExtrude","CAP_EDGE",EDGE,{"disambiguationData":[OSD([subQ4,subQ3])],"isStart":false})}),"instanceName":"1"})});}
            var Q1;
            {var subQ0=sQuery(id+"F6.wireOp",EDGE,"E7");var subQ1=sQuery(id+"F6.wireOp",EDGE,"E6.right");var subQ2=sQuery(id+"F6.wireOp",EDGE,"E3.2");Q1=makeQuery(id+"F31.boolean.opBoolean","SPLIT",EDGE,{"disambiguationData":[TD([makeQuery(id+"F23.opPattern","COPY",FACE,{"derivedFrom":makeQuery(id+"F7.boolean.opBoolean","COPY",FACE,{"derivedFrom":makeQuery(id+"F7.opExtrude","SWEPT_FACE",FACE,{"disambiguationData":[OSD([subQ1])]})}),"instanceName":"1"})])],"derivedFrom":makeQuery(id+"F23.opPattern","COPY",EDGE,{"derivedFrom":makeQuery(id+"F7.boolean.opBoolean","COPY",EDGE,{"derivedFrom":makeQuery(id+"F7.opExtrude","CAP_EDGE",EDGE,{"disambiguationData":[OSD([subQ2,subQ0])],"isStart":false})}),"instanceName":"1"})});}
            chamfer(context, id + "F32", {"entities" : qUnion([Q0, Q1]), "width" : 2 * mm, "tangentPropagation" : true});
        }
        {
            var Q0;
            Q0=makeQuery(id+"F31.boolean.opBoolean","COPY",EDGE,{"derivedFrom":makeQuery(id+"F31.opExtrude","CAP_EDGE",EDGE,{"disambiguationData":[OSD([sQuery(id+"F30.wireOp",EDGE,"E80.left")])],"isStart":false})});
            var Q1;
            Q1=makeQuery(id+"F31.boolean.opBoolean","COPY",EDGE,{"derivedFrom":makeQuery(id+"F31.opExtrude","CAP_EDGE",EDGE,{"disambiguationData":[OSD([sQuery(id+"F30.wireOp",EDGE,"E80.right")])],"isStart":false})});
            fillet(context, id + "F33", {"entities" : qUnion([Q0, Q1]), "radius" : 4 * mm, "tangentPropagation" : true, "allowEdgeOverflow" : false});
        }
        {
            var Q0;
            Q0=makeQuery(id+"F26.opExtrude","CAP_FACE",FACE,{"disambiguationData":[OSD([sQuery(id+"F0.wireOp",EDGE,"E0.bottom"),sQuery(id+"F0.wireOp",EDGE,"E0.top"),sQuery(id+"F0.wireOp",EDGE,"E0.right"),sQuery(id+"F6.wireOp",EDGE,"E3.0"),sQuery(id+"F6.wireOp",EDGE,"E3.1"),sQuery(id+"F6.wireOp",EDGE,"E3.2"),sQuery(id+"F6.wireOp",EDGE,"E5.top"),sQuery(id+"F6.wireOp",EDGE,"E5.right"),sQuery(id+"F6.wireOp",EDGE,"E6.top"),sQuery(id+"F6.wireOp",EDGE,"E6.right"),sQuery(id+"F6.wireOp",EDGE,"E7"),sQuery(id+"F6.wireOp",EDGE,"E8"),sQuery(id+"F25.wireOp",EDGE,"E73"),sQuery(id+"F25.wireOp",EDGE,"E74")])],"isStart":false});
            var sketch = newSketch(context, id + "F34", { "sketchPlane" : qUnion([Q0])});
            skLineSegment(sketch, "E81", {"start": v(156, 32.5) * mm, "end": v(163.5, 40) * mm, "construction": true});
            skLineSegment(sketch, "E82", {"start": v(163.5, 40) * mm, "end": v(159.5, 36) * mm, "construction": true});
            skLineSegment(sketch, "E83", {"start": v(156, -32.5) * mm, "end": v(163.5, -40) * mm, "construction": true});
            skLineSegment(sketch, "E84", {"start": v(163.5, -40) * mm, "end": v(159.5, -36) * mm, "construction": true});
            skSolve(sketch);
        }
        {
            var Q0;
            Q0=sQuery(id+"F34.wireOp",VERTEX,"E84.end");
            var Q1;
            Q1=sQuery(id+"F34.wireOp",VERTEX,"E82.end");
            var Q2;
            Q2=makeQuery(id+"F23.opPattern","COPY",BODY,{"derivedFrom":makeQuery(id+"F1.opExtrude","SWEPT_BODY",BODY,{"disambiguationData":[OSD([sQuery(id+"F0.wireOp",EDGE,"E0.bottom"),sQuery(id+"F0.wireOp",EDGE,"E0.top"),sQuery(id+"F0.wireOp",EDGE,"E0.left"),sQuery(id+"F0.wireOp",EDGE,"E0.right")])]}),"instanceName":"1"});
            hole(context, id + "F35", {"style" : HoleStyle.C_BORE, "endStyle" : HoleEndStyle.BLIND, "holeDiameter" : 2 * mm, "cBoreDiameter" : 2.8 * mm, "cBoreDepth" : 19 * mm, "majorDiameter" : 5 * mm, "holeDepth" : 19.5 * mm, "isTappedThrough" : true, "tappedDepth" : 12 * mm, "tapClearance" : 3, "startFromSketch" : true, "locations" : qUnion([Q0, Q1]), "scope" : qUnion([Q2])});
        }
    });
